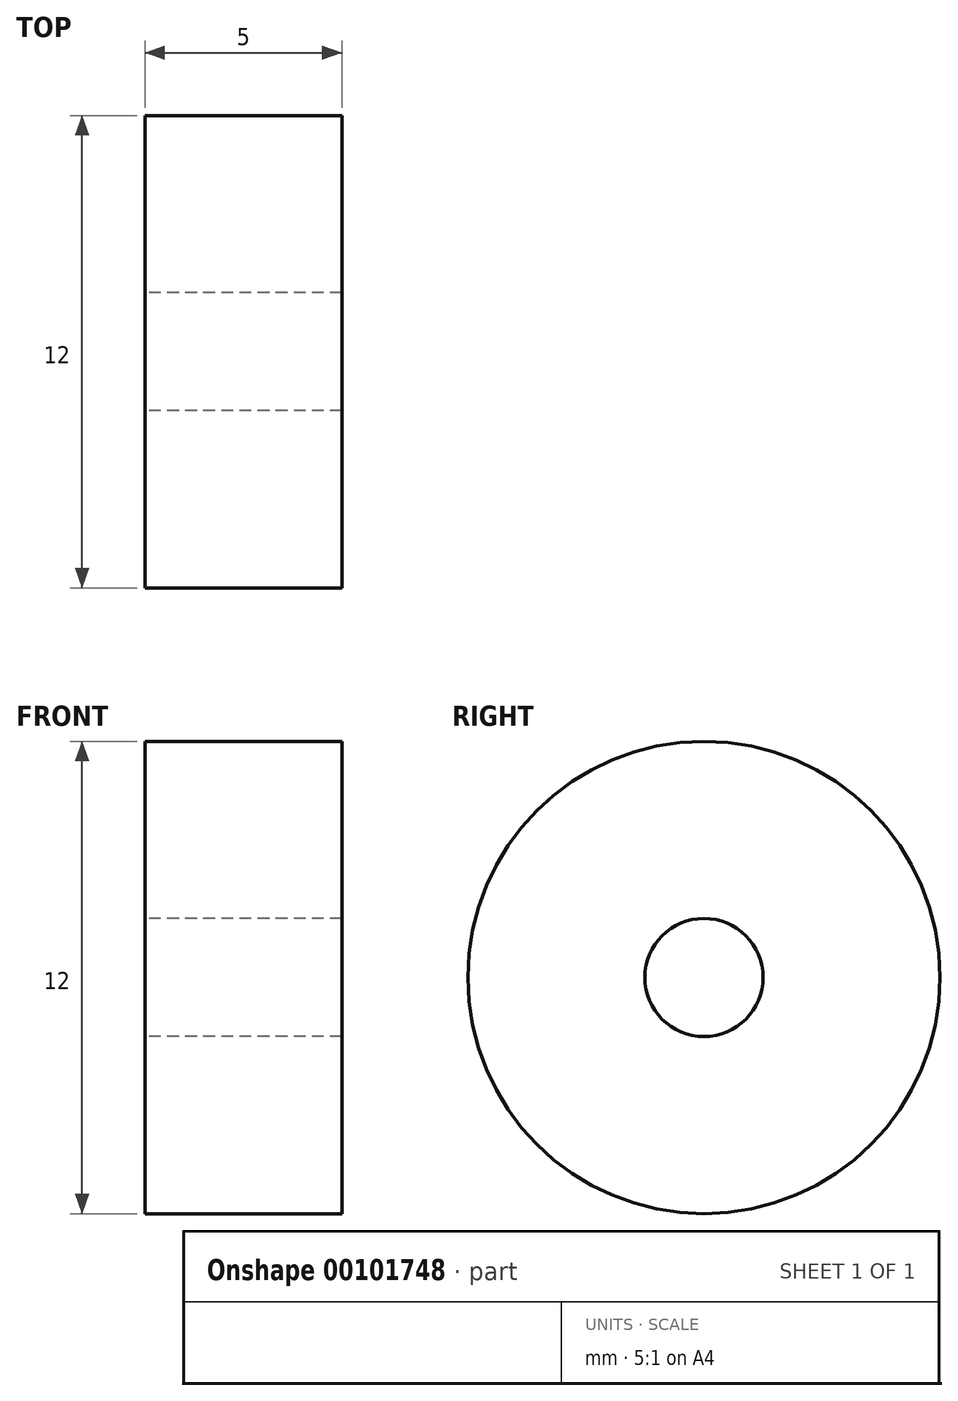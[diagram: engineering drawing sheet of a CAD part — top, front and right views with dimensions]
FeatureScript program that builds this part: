
annotation { "Feature Type Name" : "Feature", "Feature Type Description" : "" }
export const myFeature = defineFeature(function(context is Context, id is Id, definition is map)
    precondition{}
    {
        {
            var Q0;
            Q0=qCreatedBy(makeId("Right.planeOp"),FACE);
            var sketch = newSketch(context, id + "F0", { "sketchPlane" : qUnion([Q0])});
            skCircle(sketch, "E0", {"center": v(0, 0) * mm, "radius": 6 * mm});
            skCircle(sketch, "E1", {"center": v(0, 0) * mm, "radius": 1.5 * mm});
            skSolve(sketch);
        }
        {
            var Q0;
            Q0=makeQuery(id+"F0.imprint","IMPRINT",FACE,{"disambiguationData":[TD([[makeQuery(id+"F0.imprint","IMPRINT",EDGE,{"derivedFrom":sQuery(id+"F0.wireOp",EDGE,"E0")}),1.0]])]});
            extrude(context, id + "F1", {"entities" : qUnion([Q0]), "depth" : 5 * mm});
        }
    });
